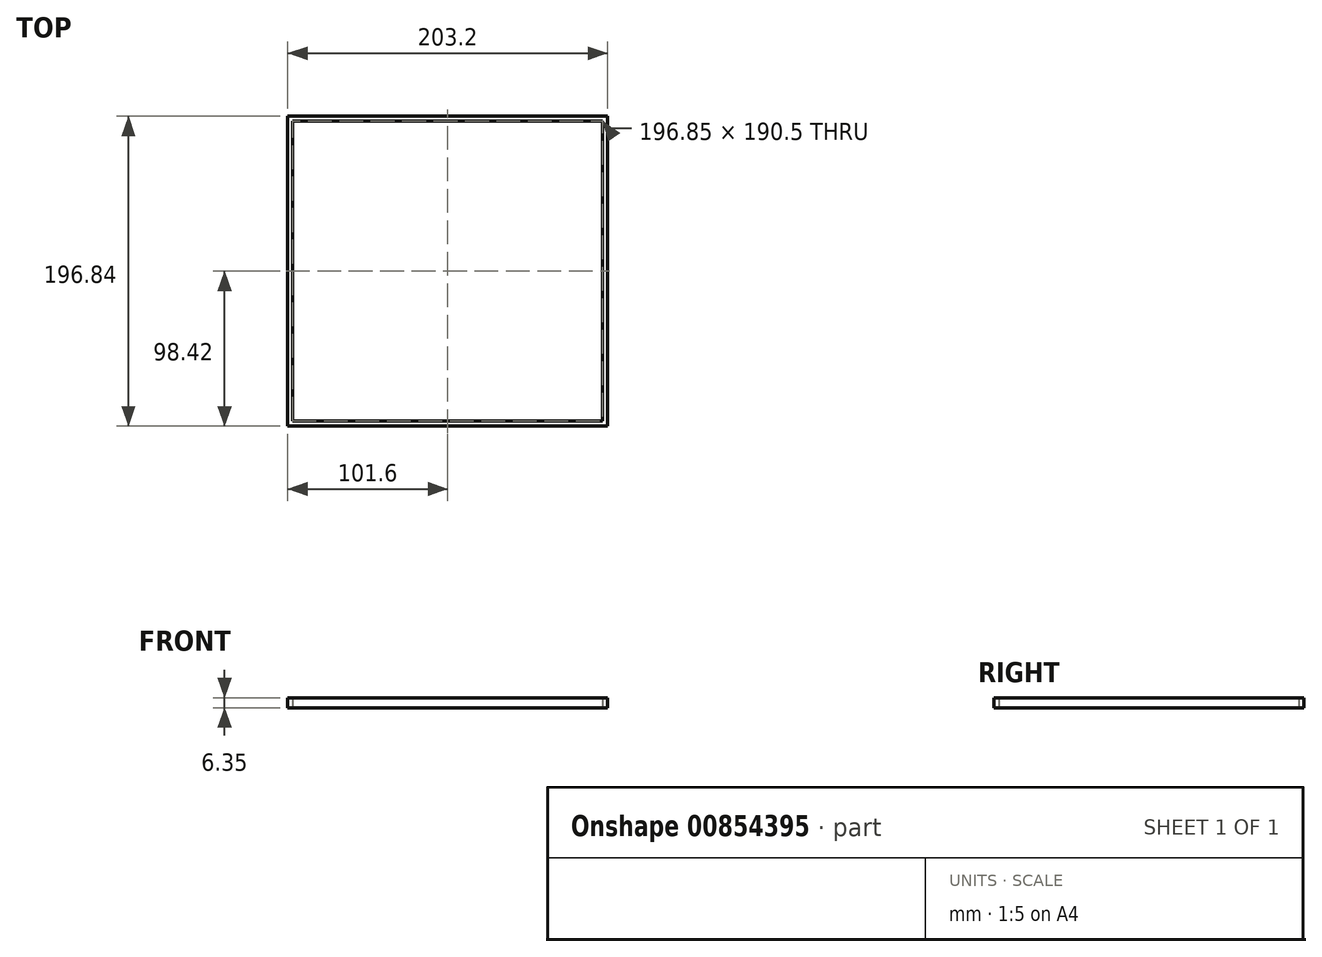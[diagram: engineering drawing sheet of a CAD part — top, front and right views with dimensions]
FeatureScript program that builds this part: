
annotation { "Feature Type Name" : "Feature", "Feature Type Description" : "" }
export const myFeature = defineFeature(function(context is Context, id is Id, definition is map)
    precondition{}
    {
        {
            var Q0;
            Q0=qCreatedBy(makeId("Top.planeOp"),FACE);
            var sketch = newSketch(context, id + "F0", { "sketchPlane" : qUnion([Q0])});
            skLineSegment(sketch, "E0.bottom", {"start": v(101.6, -98.42) * mm, "end": v(-101.6, -98.43) * mm});
            skLineSegment(sketch, "E0.top", {"start": v(101.6, 98.43) * mm, "end": v(-101.6, 98.42) * mm});
            skLineSegment(sketch, "E0.left", {"start": v(101.6, -98.42) * mm, "end": v(101.6, 98.43) * mm});
            skLineSegment(sketch, "E0.right", {"start": v(-101.6, -98.43) * mm, "end": v(-101.6, 98.43) * mm});
            skPoint(sketch, "E0.middle", {"position": v(0, 0) * mm});
            skLineSegment(sketch, "E1.bottom", {"start": v(98.43, -95.25) * mm, "end": v(-98.43, -95.25) * mm});
            skLineSegment(sketch, "E1.top", {"start": v(98.43, 95.25) * mm, "end": v(-98.43, 95.25) * mm});
            skLineSegment(sketch, "E1.left", {"start": v(98.43, -95.25) * mm, "end": v(98.43, 95.25) * mm});
            skLineSegment(sketch, "E1.right", {"start": v(-98.43, -95.25) * mm, "end": v(-98.43, 95.25) * mm});
            skSolve(sketch);
        }
        {
            var Q0;
            Q0 = qSketchRegion(id + "F0", true);
            extrude(context, id + "F1", {"entities" : qUnion([Q0]), "depth" : 6.35 * mm, "offsetDistance" : 25.4 * mm});
        }
    });
